# Revit family: Water_Closet_Support-Jay_R.Smith-(0532FY_0544FY)_Series
name_source: partatom
category: Mechanical Equipment
units: mm (PartAtom-declared; Revit-internal decimal feet)

## family parameters
Always vertical = No
Classification = None
Cut with Voids When Loaded = No
OmniClass Number = 23.70.00.00
OmniClass Title = Waste Management
Part Type = Normal
Room Calculation Point = No
Round Connector Dimension = Use Diameter
Shared = Yes
Work Plane-Based = Yes

## types (4) — shared parameters
Adjustable Height = 8 3/4"
Adjustable Height Constraint = 8 3/4"
Assembly Code = D2030400
CW Connection = No
Coupling Diameter = 4"
Coupling Inlet Connection Description = 4" No HUB Coupling Inlet Connection
Default Elevation = 0"
Description = Floor-Mount Frame for Hub and Spigot System
Finish = Cast Iron-Jay R Smith-Duco Coated
HW Connection = No
Height = 17 1/2"
Installation Type = Floor Mounted
Manufacturer = Jay R Smith
Material = Cast Iron-Jay R Smith-Duco Coated
Nipple Material = ABS-Jay R Smith-Black
Product Documentation Link = https://www.jrsmith.com
Product Page URL = https://www.jrsmith.com
Screw Material = Metal-Jay R Smith-Stainless Steel
Type Comments = Water Closet Support
URL = http://www.jrsmith.com
Vent Connection = Yes
Wall Thickness Adjustable = 8 3/4"
Waste Connection = Yes
Width = 18 1/2"
zero-valued in all types: CWFU, HWFU, WFU

## per-type parameters (varying)
| type | A Dimension | A Dimension Radius | A Outlet Connection Description | B Dimension | B Vent Connection Description | E Dimension | Vent Connection Diameter | Waste Connection Diameter | Waste Connection Radius |
| 0532FY | 3" | 1 1/2" | 3" No HUB Outlet Connection A | 2" | 2" Vent Connection B | 3" | 2" | 3" | 1 1/2" |
| 0533FY | 3" | 1 1/2" | 3" No HUB Outlet Connection A | 3" | 3" Vent Connection B | 3" | 3" | 3" | 1 1/2" |
| 0542FY | 4" | 2" | 4" No HUB Outlet Connection A | 2" | 2" Vent Connection B | 3 1/2" | 2" | 4" | 2" |
| 0544FY | 4" | 2" | 4" No HUB Outlet Connection A | 4" | 4" Vent Connection B | 3 1/2" | 4" | 4" | 2" |

note: column(s) folded — value = type name in every type: Model

## geometry (parser evidence)
native form markers: Sweep x11
no freeform markers — native parametric forms only
